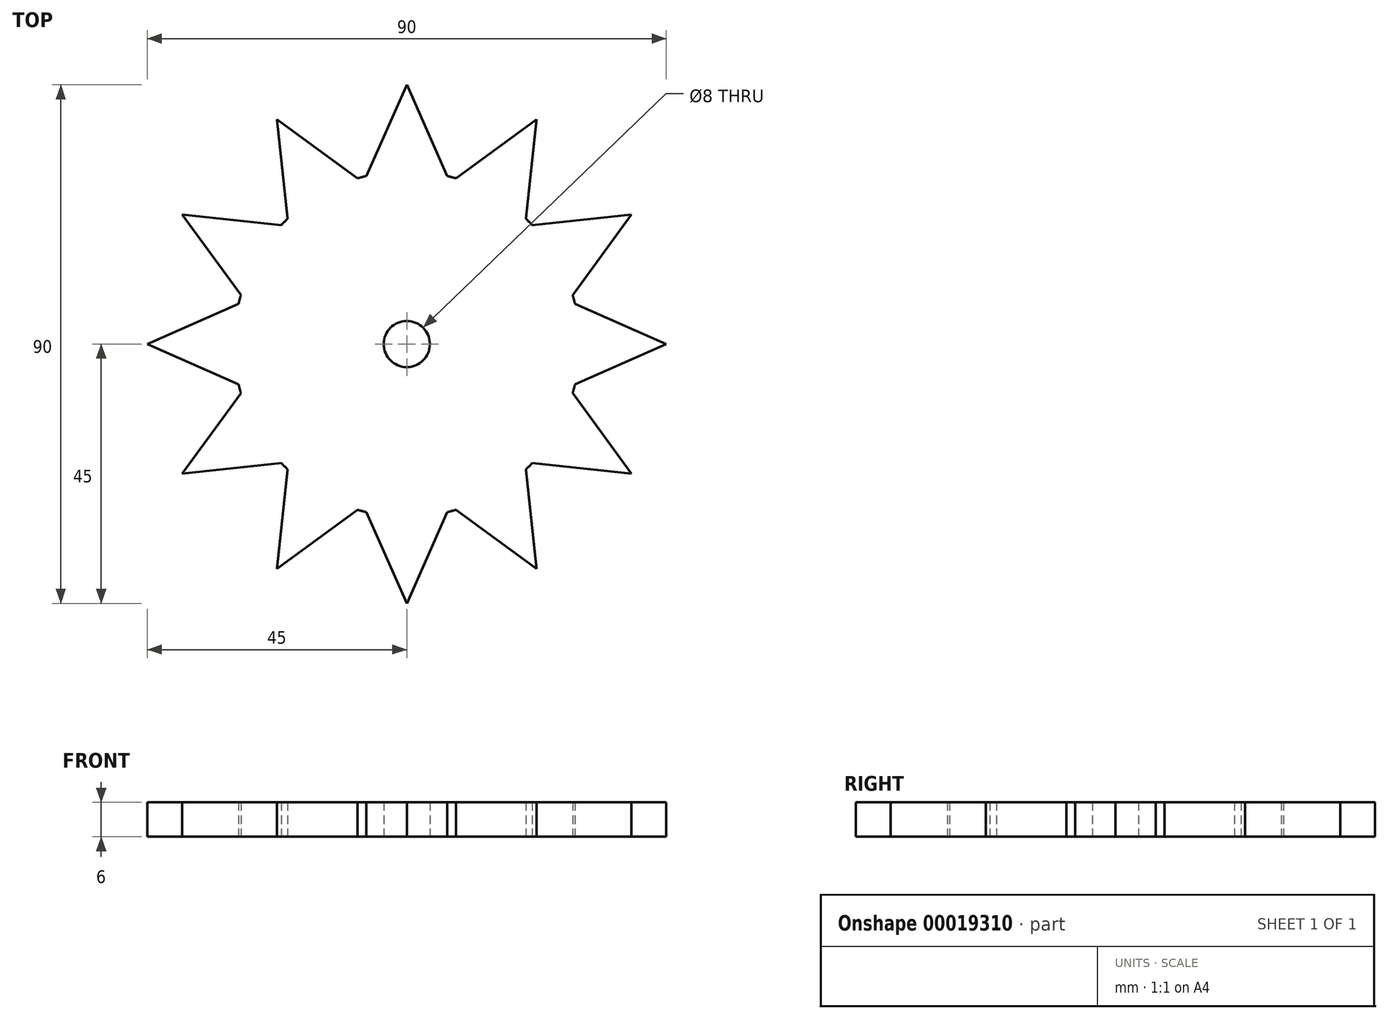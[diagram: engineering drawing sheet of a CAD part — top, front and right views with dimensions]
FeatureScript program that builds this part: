
annotation { "Feature Type Name" : "Feature", "Feature Type Description" : "" }
export const myFeature = defineFeature(function(context is Context, id is Id, definition is map)
    precondition{}
    {
        {
            var Q0;
            Q0=qCreatedBy(makeId("Top.planeOp"),FACE);
            var sketch = newSketch(context, id + "F0", { "sketchPlane" : qUnion([Q0])});
            skArc(sketch, "E0", {"start": v(-7, 29.17) * mm, "mid": v(0, -30) * mm, "end": v(7, 29.17) * mm});
            skLineSegment(sketch, "E1", {"start": v(-7, 29.17) * mm, "end": v(0, 45) * mm});
            skLineSegment(sketch, "E2", {"start": v(0, 45) * mm, "end": v(7, 29.17) * mm});
            skCircle(sketch, "E3", {"center": v(0, 0) * mm, "radius": 4 * mm});
            skSolve(sketch);
        }
        {
            var Q0;
            Q0=qSketchRegion(id+"F0",true);
            extrude(context, id + "F1", {"entities" : qUnion([Q0]), "depth" : 6 * mm});
        }
        {
            var Q0;
            Q0=makeQuery(id+"F1.opExtrude","SWEPT_BODY",BODY,{"disambiguationData":[OSD([sQuery(id+"F0.wireOp",EDGE,"E0"),sQuery(id+"F0.wireOp",EDGE,"E1"),sQuery(id+"F0.wireOp",EDGE,"E2"),sQuery(id+"F0.wireOp",EDGE,"E3")])]});
            var Q1;
            Q1=makeQuery(id+"F1.opExtrude","CAP_EDGE",EDGE,{"disambiguationData":[OSD([sQuery(id+"F0.wireOp",EDGE,"E0")])],"isStart":false});
            circularPattern(context, id + "F2", {"operationType" : NewBodyOperationType.ADD, "entities" : qUnion([Q0]), "axis" : qUnion([Q1]), "angle" : 30 * degree, "instanceCount" : round(13)});
        }
    });
